# Revit family: Zaniboni-Gem-4R
name_source: partatom
category: Lighting Fixtures
revit_build: Autodesk Revit 2016 (Build: 20150220_1215(x64)
units: mm (PartAtom-declared; Revit-internal decimal feet)

## family parameters
Cut with Voids When Loaded = No
Host = Face
Light Source = Yes
Part Type = Normal
Room Calculation Point = No
Round Connector Dimension = Use Diameter
Shared = No

## types (2) — shared parameters
Assembly Code = E1020300
Beam = 24°
Body Finish = ZBN - Metal Matte Black
CRI = 80
Color Filter = 16777215
Default Elevation = 48"
Diameter = 1"
Dimming Lamp Color Temperature Shift = <None>
Emit Shape Visible in Rendering = No
Emit from Circle Diameter = 45/64"
Frame Finish = ZBN - Metal Matte Black
Kelvin = 2700K
Keynote = 12500
Manufacturer = Zaniboni
Mechanism Finish = ZBN - Plastic-Black
Photometric Web File = generic
Screen Finish = ZBN - Glass
Support Finish = ZBN - Metal Matte Black
Tilt Angle = 90.00°
Type Comments = GEM
URL = www.zanibonilighting.com
Voltage = 120 V
Wattage Comments = 7W

## per-type parameters (varying)
| type | Description | Dist1 |
| K0-GEM4R-0327A-2C-WS-Adapter | 0.7 inch Round W/Adapter | 1 1/4" |
| K0-GEM4R-0327A-2C-WS | 0.7 inch Round Mini-Track | 0" |

note: column(s) folded — value = type name in every type: Model

## geometry (parser evidence)
native form markers: Blend x2, Sweep x3
no freeform markers — native parametric forms only
